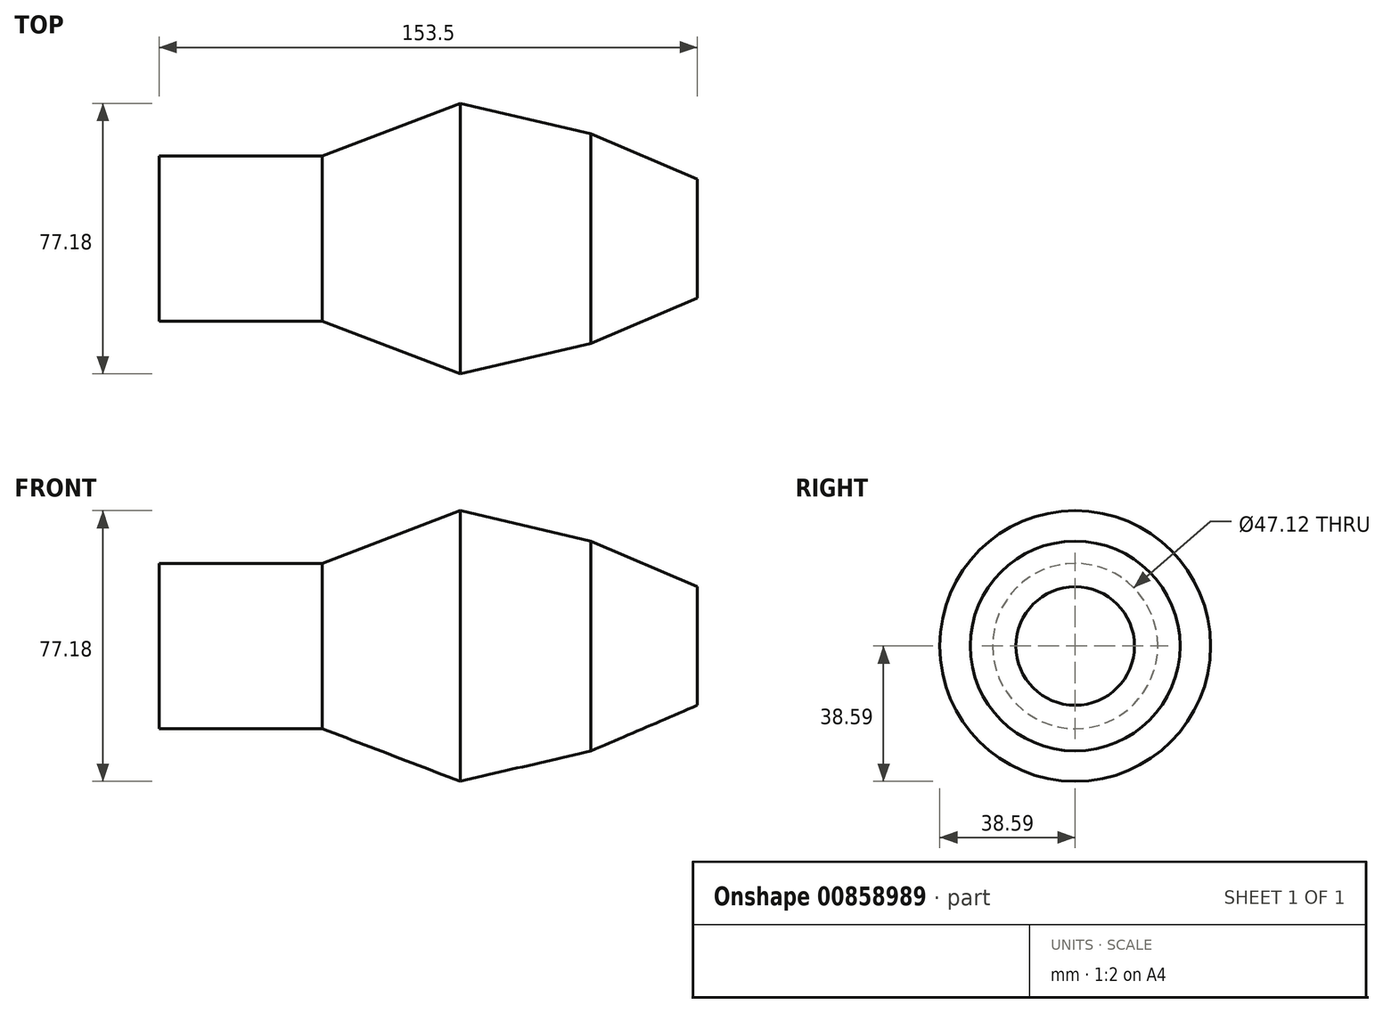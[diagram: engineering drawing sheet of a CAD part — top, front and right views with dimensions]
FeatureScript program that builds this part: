
annotation { "Feature Type Name" : "Feature", "Feature Type Description" : "" }
export const myFeature = defineFeature(function(context is Context, id is Id, definition is map)
    precondition{}
    {
        {
            var Q0;
            Q0=qCreatedBy(makeId("Front.planeOp"),FACE);
            var sketch = newSketch(context, id + "F0", { "sketchPlane" : qUnion([Q0])});
            skLineSegment(sketch, "E0", {"start": v(-67.79, 23.56) * mm, "end": v(-21.25, 23.56) * mm});
            skLineSegment(sketch, "E1", {"start": v(-21.25, 23.56) * mm, "end": v(18.07, 38.6) * mm});
            skLineSegment(sketch, "E2", {"start": v(18.07, 38.6) * mm, "end": v(55.36, 29.92) * mm});
            skLineSegment(sketch, "E3", {"start": v(55.36, 29.92) * mm, "end": v(85.7, 16.91) * mm});
            skSolve(sketch);
        }
        {
            var Q0;
            Q0=qCreatedBy(makeId("Front.planeOp"),FACE);
            var sketch = newSketch(context, id + "F1", { "sketchPlane" : qUnion([Q0])});
            skLineSegment(sketch, "E4", {"start": v(0, 0) * mm, "end": v(131.67, 0) * mm});
            skSolve(sketch);
        }
        {
            var Q0;
            Q0 = qSketchRegion(id + "F0", true);
            var Q1;
            Q1=sQuery(id+"F0.wireOp",EDGE,"E0");
            var Q2;
            Q2=sQuery(id+"F0.wireOp",EDGE,"E1");
            var Q3;
            Q3=sQuery(id+"F0.wireOp",EDGE,"E2");
            var Q4;
            Q4=sQuery(id+"F0.wireOp",EDGE,"E3");
            var Q5;
            Q5=sQuery(id+"F1.wireOp",EDGE,"E4");
            revolve(context, id + "F2", {"bodyType" : ToolBodyType.SURFACE, "operationType" : NewBodyOperationType.ADD, "surfaceOperationType" : NewSurfaceOperationType.NEW, "entities" : qUnion([Q0]), "surfaceEntities" : qUnion([Q1, Q2, Q3, Q4]), "axis" : qUnion([Q5]), "revolveType" : RevolveType.FULL});
        }
    });
